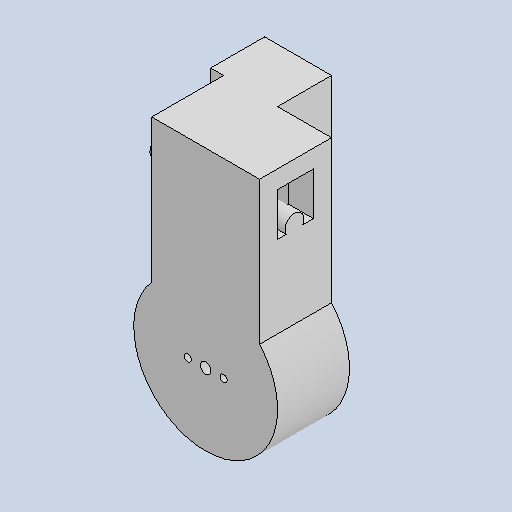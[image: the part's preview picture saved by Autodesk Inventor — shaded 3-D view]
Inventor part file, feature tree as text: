
AUTODESK INVENTOR PART (.ipt)
format: ipt  version: 2022 (Build 260153000, 153)  size: 346,624 bytes
history: native  units: in
note: dims shown in document units (in); Inventor stores cm internally (conversion verified against a paired STEP export)
features: extrude x28, sketch x28, chamfer x1
ambient origin geometry x8: Origin, YZ Plane, XZ Plane, XY Plane, X Axis, Y Axis, Z Axis, Center Point
bodies: Solid1 (feature_tree)
feature tree (57):
  extrude  "Extrusion1"  Depth=0.7874in
  extrude  "Extrusion2"  Depth=1.1811in
  extrude  "Extrusion3"  Depth=0.7874in
  extrude  "Extrusion4"  Depth=0.2362in
  extrude  "Extrusion5"  Depth=0.2362in
  extrude  "Extrusion6"  Depth=0.9055in TaperAngle=0.0deg
  extrude  "Extrusion7"  Depth=0.189in
  extrude  "Extrusion8"  Depth=0.6299in TaperAngle=0.0deg
  sketch  "Sketch11"  dims[d24=0.0984in d25=0.0591in]
  extrude  "Extrusion9"  Depth=0.0591in
  extrude  "Extrusion10"  Depth=0.0591in
  extrude  "Extrusion11"  Depth=0.3937in
  extrude  "Extrusion12"  Depth=0.1969in
  extrude  "Extrusion13"  Depth=0.1969in TaperAngle=0.0deg
  extrude  "Extrusion15"  Depth=0.1181in
  extrude  "Extrusion16"  Depth=0.1181in
  extrude  "Extrusion17"  Depth=0.3937in TaperAngle=0.0deg
  extrude  "Extrusion18"  Depth=0.3937in
  chamfer  "Chamfer2"  Distance=2.3469in
  extrude  "Extrusion27"  Depth=0.3937in TaperAngle=0.0deg
  extrude  "Extrusion31"  Depth=0.3937in TaperAngle=0.0deg
  extrude  "Extrusion32"  Depth=0.6299in TaperAngle=0.0deg
  extrude  "Extrusion33"  Depth=0.6299in TaperAngle=0.0deg
  extrude  "Extrusion34"  Depth=0.0787in
  extrude  "Extrusion35"  Depth=5.4424in TaperAngle=0.0deg
  extrude  "Extrusion36"  Depth=0.3937in
  extrude  "Extrusion37"  Depth=0.2756in TaperAngle=0.0deg
  extrude  "Extrusion38"  Depth=0.1969in TaperAngle=0.0deg
  extrude  "Extrusion40"  Depth=0.6299in
  extrude  "Extrusion41"  Depth=0.6299in
  sketch  "Sketch1"  dims[d0=0.7874in d1=1.5748in]
  sketch  "Sketch2"  dims[d2=1.1811in d3=1.9685in]
  sketch  "Sketch4"  dims[d4=0.7874in d5=0.0in d6=0.7874in]
  sketch  "Sketch6"  dims[d7=0.5906in d8=0.0in d13=0.2362in]
  sketch  "Sketch7"  dims[d14=0.9843in d15=0.2362in]
  sketch  "Sketch8"  dims[d16=0.9055in d17=0.9055in d18=0.0in]
  sketch  "Sketch9"  dims[d19=0.4724in d20=0.189in]
  sketch  "Sketch10"  dims[d21=0.189in d22=0.6299in d23=0.0in]
  sketch  "Sketch12"  dims[d26=0.0984in d27=0.0591in]
  sketch  "Sketch13"  dims[d28=0.315in d29=0.0in d30=0.3937in]
  sketch  "Sketch15"  dims[d31=0.315in d32=0.1969in]
  sketch  "Sketch16"  dims[d33=0.1969in d34=0.6225in d35=0.0in]
  sketch  "Sketch18"  dims[d36=0.0787in d37=0.1181in]
  sketch  "Sketch19"  dims[d38=0.1181in d39=0.1181in]
  sketch  "Sketch20"  dims[d40=0.315in d41=0.0in d45=0.3937in d46=0.0in]
  sketch  "Sketch21"  dims[d47=0.5906in d48=0.3937in d49=2.3469in d50=0.0in]
  sketch  "Sketch33"  dims[d51=0.3937in d52=0.0in d53=0.3937in d54=0.0in]
  sketch  "Sketch41"  dims[d56=0.9843in d57=0.3937in d58=0.0in]
  sketch  "Sketch42"  dims[d59=0.3937in d60=0.0in d70=0.6299in d71=0.0in]
  sketch  "Sketch43"  dims[d72=0.7874in d73=0.6299in d74=0.0in]
  sketch  "Sketch44"  dims[d75=1.1826in d76=0.0in d77=0.0787in]
  sketch  "Sketch45"  dims[d78=0.0787in d79=5.4424in d80=0.0in]
  sketch  "Sketch48"  dims[d81=0.315in d82=0.0787in d83=45.0deg d110=0.3937in]
  sketch  "Sketch49"  dims[d111=0.315in d112=0.2756in d113=0.0in]
  sketch  "Sketch53"  dims[d122=1.4188in d123=0.0in d124=0.1969in d125=0.0in]
  sketch  "Sketch55"  dims[d126=0.3937in d127=0.0in d128=0.6299in]
  sketch  "Sketch56"  dims[d129=0.7087in d130=0.6299in d131=0.1969in d132=0.2362in d133=0.0in d134=0.2756in d135=0.0in d136=0.2362in d137=0.0in d138=0.1417in d139=0.0in d140=0.1772in d141=0.3307in d142=0.0in d145=0.4724in d146=0.0in d147=0.1575in d148=0.0in d149=0.7205in]
